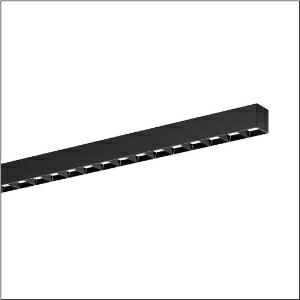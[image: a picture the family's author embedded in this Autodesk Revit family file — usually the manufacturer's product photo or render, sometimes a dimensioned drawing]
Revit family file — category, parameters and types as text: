
# Revit family: silica_r__21_51mx22tctab_4aec
name_source: partatom
category: Lighting Fixtures
units: mm (PartAtom-declared; Revit-internal decimal feet)

## family parameters
Cut with Voids When Loaded = No
Host = Face
Light Source = No
Part Type = Normal
Room Calculation Point = No
Round Connector Dimension = Use Diameter
Shared = No

## types (1)
- --- (1 x LED, 9300 lm, 80.4 W, 6500K)
    Apparent Load = 80 VA
    CIE Flux Codes = 84 100 100 100 100
    Color Rendering = 80
    Color Temperature = 6500K
    Default Elevation = 1800 mm
    Description = Silica® 21, office luminaire, primary light control with darklight reflector, of PMMA, black, CAT 2 (L<= 3000cd/m²), light emission: direct distribution, primary light characteristic: symmetric, installation type: surface-mounted, LED, rated luminous flux: 9.300lm, luminous efficacy: 110lm/W, light colour: 8tw, colour temperature: 2700..6500K, control gear: ECG DALI, with terminal, 3+2-pole, max. 2.5mm², mains connection: 220..240V, AC, 50/60Hz, rated input power: 84.5W, luminaire housing, of aluminium, jet black (RAL 9005), length: 3.004mm, width: 53mm, height: 53mm, protection rating (complete): IP20, insulation class (complete): insulation class I (protective earthing), certification: CE, permissible operating ambient temperature: 0..+35°C, standard: EN 50419, packaging unit: 1 piece
    Height = 0 mm  [stored 0 ft]
    Lamp = 1 x LED
    Lamp Light Flux = 9300 lm
    Lamp Power = 80.4 W
    Lamp count = 1
    Length = 3004 mm
    Luminous efficacy = 116 lm/W
    Manufacturer = Siteco
    ModVariant = No
    Model = 51MX22TCTAB
    Mounting Place = Ceiling
    Mounting Type = Recessed
    Number of Poles = 1
    OnlyDefault = Yes
    Power Factor = 1
    Product Name = Silica® 21
    Product group = office luminaire | ceiling recessed
    ProductGroupID = 401
    Protection Class = Protection class I
    Protection Degree = IP 20
    RLX_Detail_Level = 1
    RLX_Emergency_Light_Flux = 0 lm
    RLX_Emergency_Type = 0
    RLX_Emergency_Type_DB = No
    RlxData = <blob elided: 61421 chars, md5=c3d93673>
    Socket = socket
    Standby Power = 0 W
    System Light Flux = 9300 lm
    System Power = 80 W
    Type Comments = individual setting
    Type Image = l_1313577.jpg
    URL = http://relux.com
    VarID = @adj_089499
    Voltage = 0 V
    Weight = 0.00 kg
    Width = 53 mm

note: [stored X ft] marks values corroborated as IEEE doubles in the binary element streams (Revit-internal decimal feet)

## geometry (parser evidence)
native form markers: Blend x4, Sweep x12
no freeform markers — native parametric forms only
